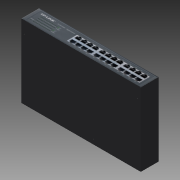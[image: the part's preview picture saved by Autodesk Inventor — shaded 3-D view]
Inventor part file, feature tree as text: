
AUTODESK INVENTOR PART (.ipt)
format: ipt  version: 2013 SP2 (Build 170200200, 200)  size: 124,928 bytes
history: native  units: mm
features: sketch x2, extrude x1, hole x1
ambient origin geometry x8: Origin, YZ Plane, XZ Plane, XY Plane, X Axis, Y Axis, Z Axis, Center Point
bodies: Solid1 (feature_tree)
feature tree (4):
  extrude  "Extrusion1"  Depth=180.0mm
  hole  "Hole1"  [1 undecoded]
  sketch  "Sketch1"  dims[d0=294.0mm d1=180.0mm]
  sketch  "Sketch3"  dims[d2=44.0mm d3=0.0mm d7=7.0mm d8=29.5mm d9=12.0mm d11=117.0mm d12=8.5mm d13=27.0mm d14=3.0mm d15=6.0mm d16=4.0mm d17=2.0mm d18=90.0deg d19=6.0mm d20=20.594885mm]
note: 1 required parameter value undecoded (feature->parameter linkage not recoverable at this tier; creation-order binding heuristic only, values carry confidence <= 0.55)
